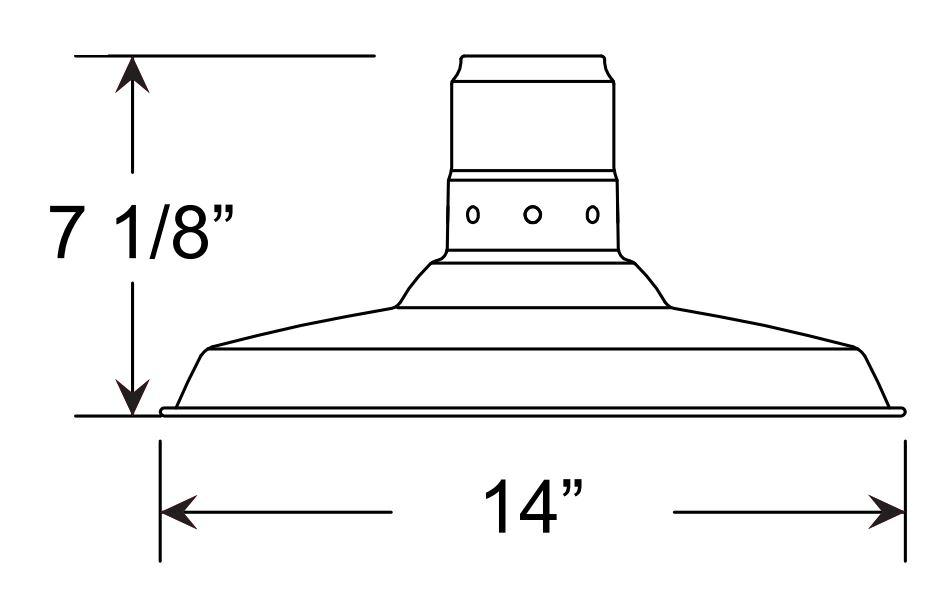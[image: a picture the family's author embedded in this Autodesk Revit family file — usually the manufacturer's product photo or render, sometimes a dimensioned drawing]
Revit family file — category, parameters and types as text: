
# Revit family: DEEP DOME_LED 10,12,16,20
name_source: partatom
category: Lighting Fixtures
units: mm (PartAtom-declared; Revit-internal decimal feet)

## family parameters
Always vertical = Yes
Cut with Voids When Loaded = No
Light Source = Yes
OmniClass Number = 23.80.70.00
OmniClass Title = Lighting
Part Type = Normal
Room Calculation Point = No
Round Connector Dimension = Use Diameter
Shared = No
Work Plane-Based = No

## types (4) — shared parameters
Body Colour = Spun aluminium
Body Material = body
Bulb = Glass
CRI = >90
Canopy Body = body
Color Filter = 16777215
Construction Material = Heavy Duty spun aluminum.
Default Elevation = 0' - 0"
Description = 120-277 Voltage
Dimming = 1%
Dimming Lamp Color Temperature Shift = <None>
Efficiency = 97-125 lumens per watt
Lamp = LED
Life = L70 50,000 hours
Load Classification = Lighting
Manufacturer = ANP Lighting
Photometric Web File = generic
Power Factor = 1
Tilt Angle = 90.00°
URL = https://www.anplighting.com
Voltage = 120 V
Warranty = 5 year limited warranty

## per-type parameters (varying)
| type | Apparent Load | DD10 | DD12 | DD16 | DD20 | Fixture Diameter | Fixture Height | Wattage Comments | Weight | a | b |
| DD10 | 10 VA | Yes | No | No | No | 0' - 10" | 0' - 6" | 10W | 1.0 lb | 0' - 9" | 0' - 2" |
| DD12 | 16 VA | No | Yes | No | No | 1' - 0" | 0' - 7 1/4" | 16W | 2.0 lb | 0' - 9 1/4" | 0' - 3" |
| DD16 | 24 VA | No | No | Yes | No | 1' - 4" | 0' - 9 3/4" | 24 W | 4.0 lbs | 0' - 10 3/4" | 0' - 5 1/4" |
| DD20 | 24 VA | No | No | No | Yes | 1' - 8" | 1' - 0 1/4" | 24 W | 6 lb | 1' - 0 1/4" | 0' - 7" |

note: column(s) folded — value = type name in every type: Model

## geometry (parser evidence)
native form markers: Sweep x54
no freeform markers — native parametric forms only
